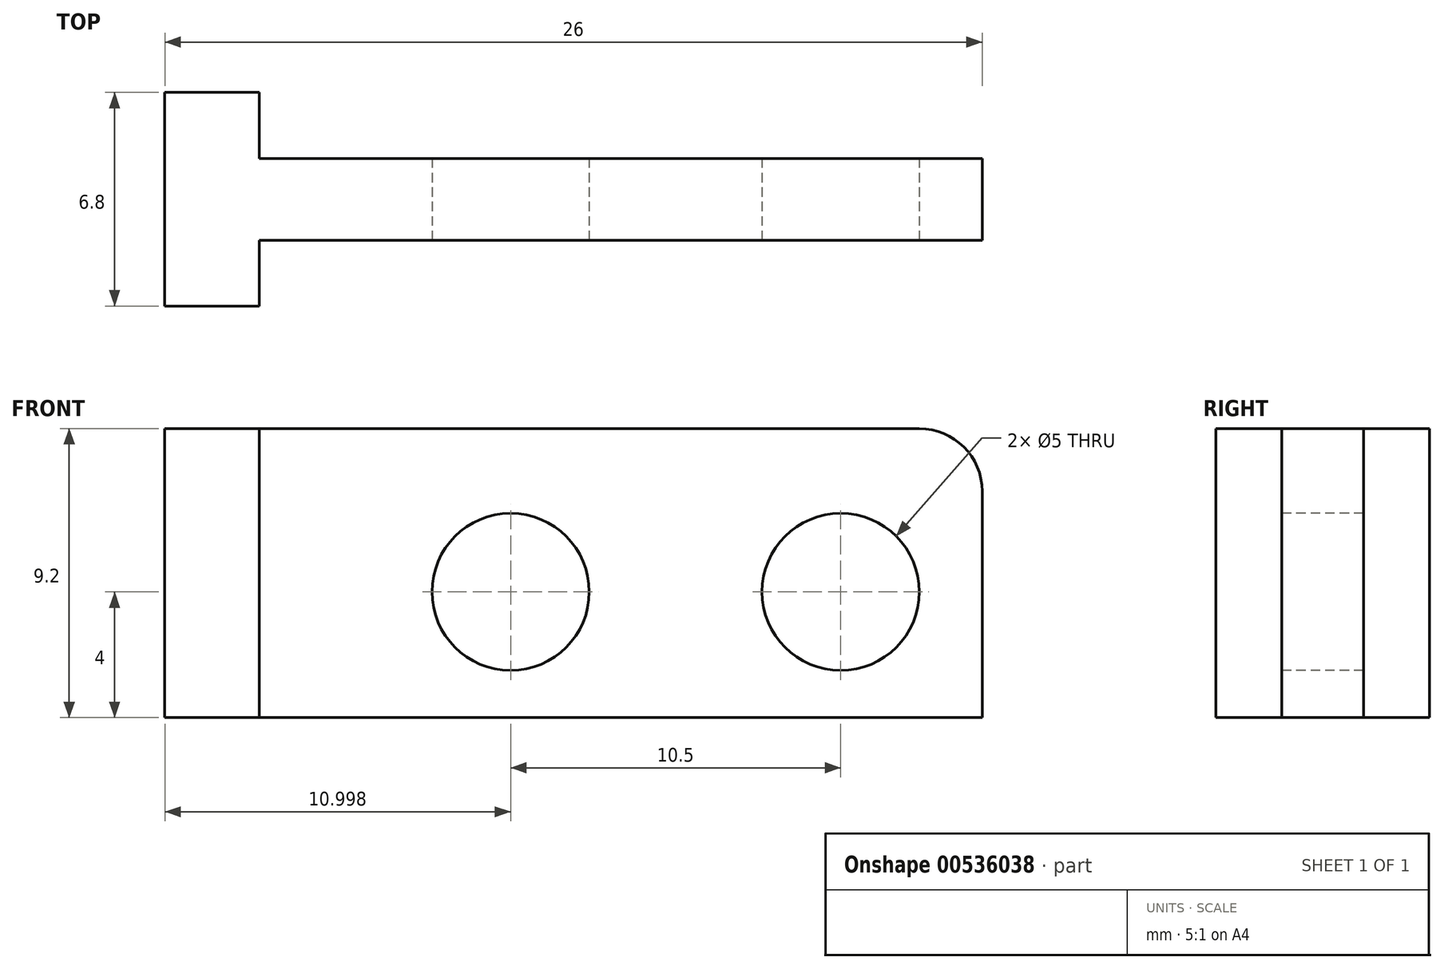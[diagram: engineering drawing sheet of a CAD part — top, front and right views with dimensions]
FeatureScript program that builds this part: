
annotation { "Feature Type Name" : "Feature", "Feature Type Description" : "" }
export const myFeature = defineFeature(function(context is Context, id is Id, definition is map)
    precondition{}
    {
        {
            var Q0;
            Q0=qCreatedBy(makeId("Top.planeOp"),FACE);
            var sketch = newSketch(context, id + "F0", { "sketchPlane" : qUnion([Q0])});
            skLineSegment(sketch, "E0.bottom", {"start": v(-39.35, 2.73) * mm, "end": v(-36.35, 2.73) * mm});
            skLineSegment(sketch, "E0.top", {"start": v(-39.35, 9.53) * mm, "end": v(-36.35, 9.53) * mm});
            skLineSegment(sketch, "E0.left", {"start": v(-39.35, 2.73) * mm, "end": v(-39.35, 9.53) * mm});
            skLineSegment(sketch, "E0.right", {"start": v(-36.35, 2.73) * mm, "end": v(-36.35, 9.53) * mm});
            skLineSegment(sketch, "E1", {"start": v(-36.35, 7.43) * mm, "end": v(-13.35, 7.43) * mm});
            skLineSegment(sketch, "E2", {"start": v(-13.35, 4.83) * mm, "end": v(-36.35, 4.83) * mm});
            skLineSegment(sketch, "E3", {"start": v(-13.35, 7.43) * mm, "end": v(-13.35, 4.83) * mm});
            skSolve(sketch);
        }
        {
            var Q0;
            {var subQ1=sQuery(id+"F0.wireOp",EDGE,"E0.bottom");Q0=makeQuery(id+"F0.imprint","IMPRINT",FACE,{"disambiguationData":[TD([[makeQuery(id+"F0.imprint","IMPRINT",EDGE,{"derivedFrom":subQ1}),1.0]])]});}
            var Q1;
            {var subQ0=sQuery(id+"F0.wireOp",EDGE,"E1");Q1=makeQuery(id+"F0.imprint","IMPRINT",FACE,{"disambiguationData":[TD([[makeQuery(id+"F0.imprint","IMPRINT",EDGE,{"derivedFrom":subQ0}),-1.0]])]});}
            extrude(context, id + "F1", {"entities" : qUnion([Q0, Q1]), "depth" : 9.2 * mm, "offsetDistance" : 25 * mm});
        }
        {
            var Q0;
            Q0=makeQuery(id+"F1.opExtrude","SWEPT_FACE",FACE,{"disambiguationData":[OSD([sQuery(id+"F0.wireOp",EDGE,"E2")])]});
            var sketch = newSketch(context, id + "F2", { "sketchPlane" : qUnion([Q0])});
            skCircle(sketch, "E4", {"center": v(-28.35, 4) * mm, "radius": 2.5 * mm});
            skCircle(sketch, "E5", {"center": v(-17.85, 4) * mm, "radius": 2.5 * mm});
            skSolve(sketch);
        }
        {
            var Q0;
            Q0=makeQuery(id+"F2.imprint","IMPRINT",FACE,{"disambiguationData":[TD([[makeQuery(id+"F2.imprint","IMPRINT",EDGE,{"derivedFrom":sQuery(id+"F2.wireOp",EDGE,"E4")}),1.0]])]});
            var Q1;
            Q1=makeQuery(id+"F2.imprint","IMPRINT",FACE,{"disambiguationData":[TD([[makeQuery(id+"F2.imprint","IMPRINT",EDGE,{"derivedFrom":sQuery(id+"F2.wireOp",EDGE,"E5")}),1.0]])]});
            extrude(context, id + "F3", {"entities" : qUnion([Q0, Q1]), "operationType" : NewBodyOperationType.REMOVE, "oppositeDirection" : true, "depth" : 3.1 * mm, "offsetDistance" : 25 * mm});
        }
        {
            var Q0;
            Q0=makeQuery(id+"F1.opExtrude","CAP_EDGE",EDGE,{"disambiguationData":[OSD([sQuery(id+"F0.wireOp",EDGE,"E3")])],"isStart":false});
            fillet(context, id + "F4", {"entities" : qUnion([Q0]), "radius" : 2 * mm, "tangentPropagation" : true, "allowEdgeOverflow" : false});
        }
    });
